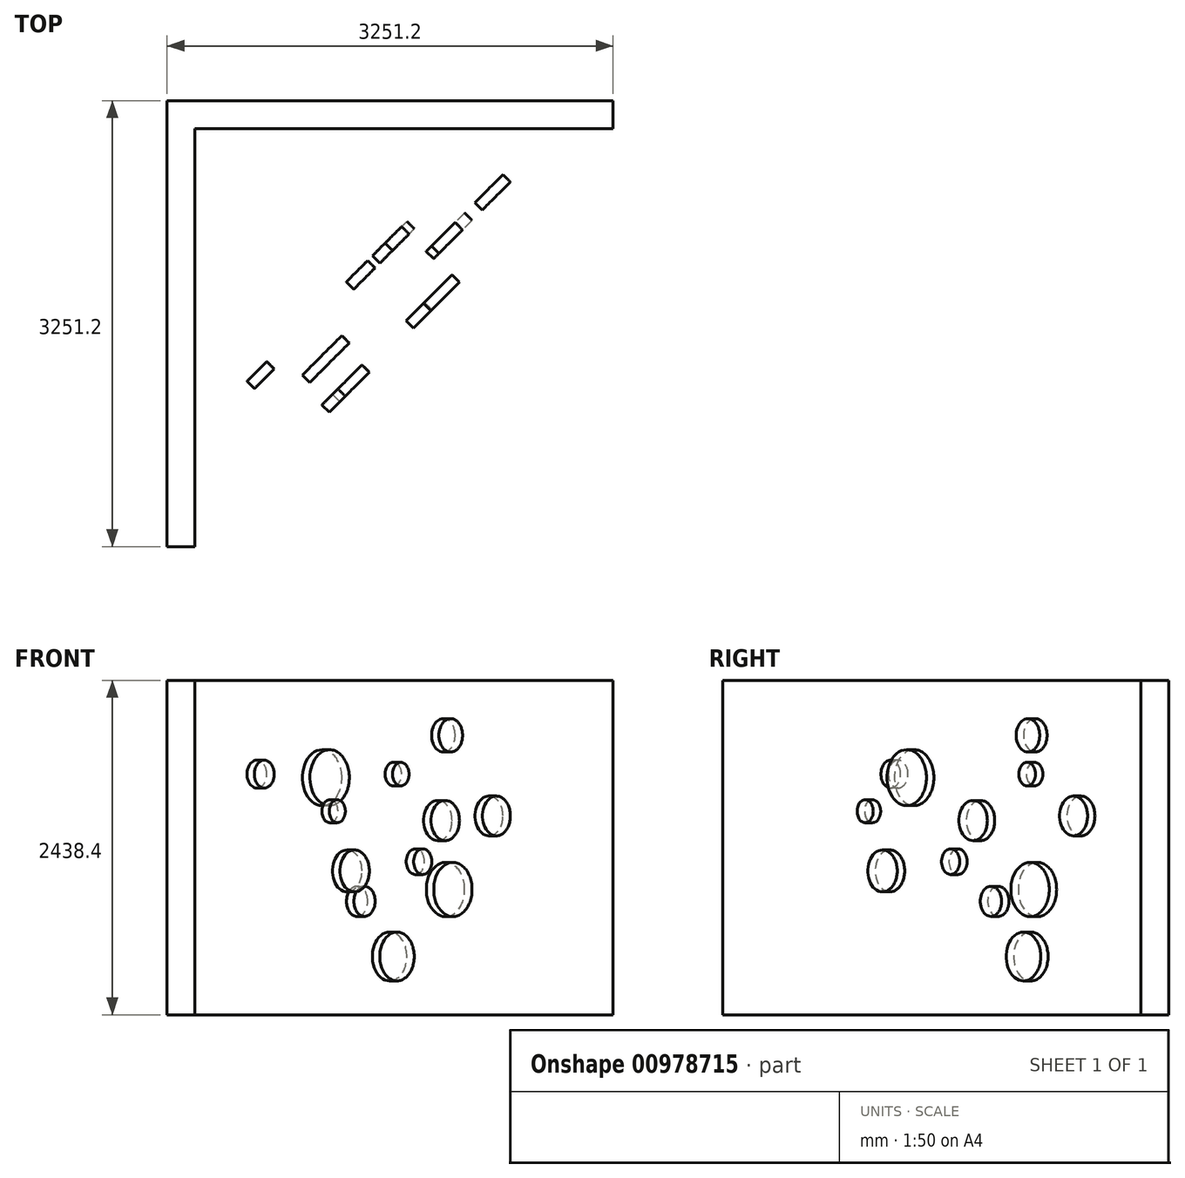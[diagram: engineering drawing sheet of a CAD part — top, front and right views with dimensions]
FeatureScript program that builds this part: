
annotation { "Feature Type Name" : "Feature", "Feature Type Description" : "" }
export const myFeature = defineFeature(function(context is Context, id is Id, definition is map)
    precondition{}
    {
        {
            var Q0;
            Q0=qCreatedBy(makeId("Top.planeOp"),FACE);
            var sketch = newSketch(context, id + "F0", { "sketchPlane" : qUnion([Q0])});
            skLineSegment(sketch, "E0.bottom", {"start": v(1524, 1524) * mm, "end": v(-1524, 1524) * mm});
            skLineSegment(sketch, "E0.top", {"start": v(1524, -1524) * mm, "end": v(-1524, -1524) * mm});
            skLineSegment(sketch, "E0.left", {"start": v(1524, 1524) * mm, "end": v(1524, -1524) * mm});
            skLineSegment(sketch, "E0.right", {"start": v(-1524, 1524) * mm, "end": v(-1524, -1524) * mm});
            skPoint(sketch, "E0.middle", {"position": v(0, 0) * mm});
            skSolve(sketch);
        }
        {
            var Q0;
            Q0=makeQuery(id+"F0.imprint","IMPRINT",FACE,{"disambiguationData":[TD([[makeQuery(id+"F0.imprint","IMPRINT",EDGE,{"derivedFrom":sQuery(id+"F0.wireOp",EDGE,"E0.bottom")}),1.0]])]});
            var sketch = newSketch(context, id + "F1", { "sketchPlane" : qUnion([Q0])});
            skLineSegment(sketch, "E1.0", {"start": v(-1524, 1524) * mm, "end": v(-1524, -1524) * mm, "construction": true});
            skLineSegment(sketch, "E2.0", {"start": v(1524, -1524) * mm, "end": v(-1524, -1524) * mm, "construction": true});
            skLineSegment(sketch, "E3.0", {"start": v(1524, 1524) * mm, "end": v(-1524, 1524) * mm, "construction": true});
            skLineSegment(sketch, "E4.bottom", {"start": v(-1524, -1524) * mm, "end": v(-1727.2, -1524) * mm});
            skLineSegment(sketch, "E4.top", {"start": v(-1524, 1727.2) * mm, "end": v(-1727.2, 1727.2) * mm});
            skLineSegment(sketch, "E4.left", {"start": v(-1524, -1524) * mm, "end": v(-1524, 1524) * mm});
            skLineSegment(sketch, "E4.right", {"start": v(-1727.2, -1524) * mm, "end": v(-1727.2, 1727.2) * mm});
            skLineSegment(sketch, "E5.bottom", {"start": v(-1727.2, 1727.2) * mm, "end": v(1524, 1727.2) * mm});
            skLineSegment(sketch, "E5.top", {"start": v(-1524, 1524) * mm, "end": v(1524, 1524) * mm});
            skLineSegment(sketch, "E5.left", {"start": v(-1727.2, 1727.2) * mm, "end": v(-1727.2, 1524) * mm});
            skLineSegment(sketch, "E5.right", {"start": v(1524, 1727.2) * mm, "end": v(1524, 1524) * mm});
            skSolve(sketch);
        }
        {
            var Q0;
            Q0 = qSketchRegion(id + "F1", true);
            extrude(context, id + "F2", {"entities" : qUnion([Q0]), "depth" : 2438.4 * mm, "offsetDistance" : 25.4 * mm});
        }
        {
            var Q0;
            Q0=makeQuery(id+"F2.opExtrude","CAP_VERTEX",VERTEX,{"disambiguationData":[OSD([sQuery(id+"F0.wireOp",EDGE,"E0.top"),sQuery(id+"F1.wireOp",EDGE,"E4.bottom"),sQuery(id+"F1.wireOp",EDGE,"E4.left")])],"isStart":false});
            var Q1;
            Q1=makeQuery(id+"F2.opExtrude","CAP_VERTEX",VERTEX,{"disambiguationData":[OSD([sQuery(id+"F0.wireOp",EDGE,"E0.left"),sQuery(id+"F1.wireOp",EDGE,"E5.top"),sQuery(id+"F1.wireOp",EDGE,"E5.right")])],"isStart":false});
            var Q2;
            Q2=sQuery(id+"F0.wireOp",VERTEX,"E0.bottom.start");
            cPlane(context, id + "F3", {"entities" : qUnion([Q0, Q1, Q2]), "cplaneType" : CPlaneType.THREE_POINT, "offset" : 25.4 * mm, "width" : 152.4 * mm, "height" : 152.4 * mm});
        }
        {
            var Q0;
            Q0=qCreatedBy(id+"F3.planeOp",FACE);
            cPlane(context, id + "F4", {"entities" : qUnion([Q0]), "cplaneType" : CPlaneType.OFFSET, "offset" : 254 * mm, "oppositeDirection" : true, "width" : 152.4 * mm, "height" : 152.4 * mm});
        }
        {
            var Q0;
            Q0=qCreatedBy(id+"F4.planeOp",FACE);
            cPlane(context, id + "F5", {"entities" : qUnion([Q0]), "cplaneType" : CPlaneType.OFFSET, "offset" : 254 * mm, "oppositeDirection" : true, "width" : 152.4 * mm, "height" : 152.4 * mm});
        }
        {
            var Q0;
            Q0=qCreatedBy(id+"F5.planeOp",FACE);
            cPlane(context, id + "F6", {"entities" : qUnion([Q0]), "cplaneType" : CPlaneType.OFFSET, "offset" : 254 * mm, "oppositeDirection" : true, "width" : 152.4 * mm, "height" : 152.4 * mm});
        }
        {
            var Q0;
            Q0=qCreatedBy(id+"F6.planeOp",FACE);
            cPlane(context, id + "F7", {"entities" : qUnion([Q0]), "cplaneType" : CPlaneType.OFFSET, "offset" : 254 * mm, "oppositeDirection" : true, "width" : 152.4 * mm, "height" : 152.4 * mm});
        }
        {
            var Q0;
            Q0=qCreatedBy(id+"F7.planeOp",FACE);
            cPlane(context, id + "F8", {"entities" : qUnion([Q0]), "cplaneType" : CPlaneType.OFFSET, "offset" : 254 * mm, "oppositeDirection" : true, "width" : 152.4 * mm, "height" : 152.4 * mm});
        }
        {
            var Q0;
            Q0=qCreatedBy(id+"F8.planeOp",FACE);
            cPlane(context, id + "F9", {"entities" : qUnion([Q0]), "cplaneType" : CPlaneType.OFFSET, "offset" : 254 * mm, "oppositeDirection" : true, "width" : 152.4 * mm, "height" : 152.4 * mm});
        }
        {
            var Q0;
            Q0=qCreatedBy(id+"F3.planeOp",FACE);
            var sketch = newSketch(context, id + "F10", { "sketchPlane" : qUnion([Q0])});
            skCircle(sketch, "E6", {"center": v(-688.89, 1483.77) * mm, "radius": 83.28 * mm});
            skCircle(sketch, "E7", {"center": v(-510.52, 1048.55) * mm, "radius": 152.4 * mm});
            skCircle(sketch, "E8", {"center": v(424.15, 1416) * mm, "radius": 146.3 * mm});
            skCircle(sketch, "E9", {"center": v(192.26, 1116.33) * mm, "radius": 93.64 * mm});
            skSolve(sketch);
        }
        {
            var Q0;
            Q0=qCreatedBy(id+"F4.planeOp",FACE);
            var sketch = newSketch(context, id + "F11", { "sketchPlane" : qUnion([Q0])});
            skCircle(sketch, "E10", {"center": v(-514.25, 1728.8) * mm, "radius": 203.2 * mm});
            skCircle(sketch, "E11", {"center": v(756.73, 913.31) * mm, "radius": 197.82 * mm});
            skCircle(sketch, "E12", {"center": v(1204.88, 1449.62) * mm, "radius": 144.71 * mm});
            skCircle(sketch, "E13", {"center": v(734.69, 2037.36) * mm, "radius": 121.6 * mm});
            skSolve(sketch);
        }
        {
            var Q0;
            Q0 = qSketchRegion(id + "F10", true);
            extrude(context, id + "F12", {"entities" : qUnion([Q0]), "oppositeDirection" : true, "depth" : 76.2 * mm, "offsetDistance" : 25.4 * mm});
        }
        {
            var Q0;
            Q0 = qSketchRegion(id + "F11", true);
            extrude(context, id + "F13", {"entities" : qUnion([Q0]), "oppositeDirection" : true, "depth" : 76.2 * mm, "offsetDistance" : 25.4 * mm});
        }
        {
            var Q0;
            Q0=qCreatedBy(id+"F5.planeOp",FACE);
            var sketch = newSketch(context, id + "F14", { "sketchPlane" : qUnion([Q0])});
            skCircle(sketch, "E14", {"center": v(-933.13, 1754.24) * mm, "radius": 101.42 * mm});
            skCircle(sketch, "E15", {"center": v(434.82, 425) * mm, "radius": 177.8 * mm});
            skCircle(sketch, "E16", {"center": v(473.12, 1754.24) * mm, "radius": 85.32 * mm});
            skCircle(sketch, "E17", {"center": v(99.53, 827.12) * mm, "radius": 109.74 * mm});
            skSolve(sketch);
        }
        {
            var Q0;
            Q0 = qSketchRegion(id + "F14", true);
            extrude(context, id + "F15", {"entities" : qUnion([Q0]), "oppositeDirection" : true, "depth" : 76.2 * mm, "offsetDistance" : 25.4 * mm});
        }
    });
